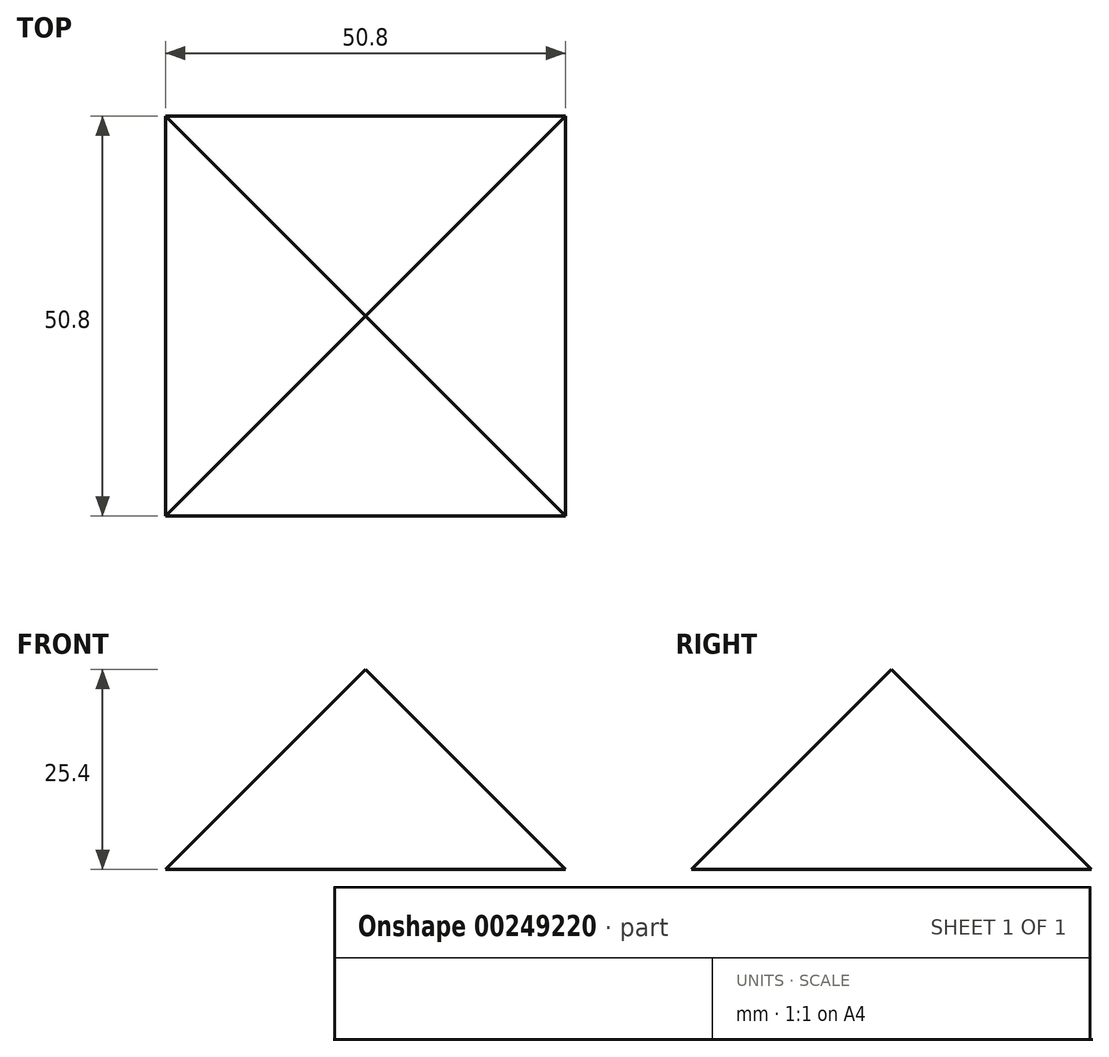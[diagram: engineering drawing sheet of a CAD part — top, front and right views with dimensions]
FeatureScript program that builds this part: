
annotation { "Feature Type Name" : "Feature", "Feature Type Description" : "" }
export const myFeature = defineFeature(function(context is Context, id is Id, definition is map)
    precondition{}
    {
        {
            var Q0;
            Q0=qCreatedBy(makeId("Top.planeOp"),FACE);
            var sketch = newSketch(context, id + "F0", { "sketchPlane" : qUnion([Q0])});
            skLineSegment(sketch, "E0", {"start": v(-77, 76.84) * mm, "end": v(75.4, 76.84) * mm});
            skLineSegment(sketch, "E1", {"start": v(75.4, 76.84) * mm, "end": v(75.4, -75.56) * mm});
            skLineSegment(sketch, "E2", {"start": v(75.4, -75.56) * mm, "end": v(-77, -75.56) * mm});
            skLineSegment(sketch, "E3", {"start": v(-77, -75.56) * mm, "end": v(-77, 76.84) * mm});
            skSolve(sketch);
        }
        {
            var Q0;
            Q0=makeQuery(id+"F0.imprint","IMPRINT",FACE,{"disambiguationData":[TD([[makeQuery(id+"F0.imprint","IMPRINT",EDGE,{"derivedFrom":sQuery(id+"F0.wireOp",EDGE,"E0")}),-1.0]])]});
            extrude(context, id + "F1", {"entities" : qUnion([Q0]), "depth" : 25.4 * mm});
        }
        {
            var Q0;
            Q0=makeQuery(id+"F1.opExtrude","CAP_FACE",FACE,{"disambiguationData":[OSD([sQuery(id+"F0.wireOp",EDGE,"E0"),sQuery(id+"F0.wireOp",EDGE,"E1"),sQuery(id+"F0.wireOp",EDGE,"E2"),sQuery(id+"F0.wireOp",EDGE,"E3")])],"isStart":false});
            chamfer(context, id + "F2", {"entities" : qUnion([Q0]), "width" : 76.2 * mm, "tangentPropagation" : true});
        }
    });
